# Revit family: Sanitary_Installation-Systems_DURAVIT-AG_DuraSystem-Actuator-Plate-WD5002
name_source: partatom
category: Generic Models
revit_build: Autodesk Revit 2018 (Build: 20180329_1100(x64)
units: mm (PartAtom-declared; Revit-internal decimal feet)

## family parameters
Can host rebar = No
Cut with Voids When Loaded = No
Host = Face
OmniClass Number = 23.31.19.00
OmniClass Title = Toilets
Part Type = Normal
Room Calculation Point = No
Round Connector Dimension = Use Diameter
Shared = No

## types (1)
- DuraSystem Actuator Plate WD5002
    BIMobject category = Installation Systems
    Date of publishing = 26/05/2020 00:00:00
    Default Elevation = 1219 mm
    Description = Actuator Plate A1, for toilet, glass white, mechanical actuation, 157x230x14 mm
    Design country = Germany
    EAN code = 4053424507316
    ETIM classification = EC012353 | Accessories bathroom accessories
    Edition number = 1
    IFC Classification = Actuator
    Installation instructions = http://pro.duravit.com
    Main material = Duravit - Metal - 00 - White Alpin
    Manufacturer = Duravit
    Manufacturer country = Germany
    Manufacturer name = DURAVIT AG
    Masterformat 2014 Code = 22 40 00
    Masterformat 2014 Description = Plumbing Fixtures
    Material main = Glass
    Model = DuraSystem Actuator Plate WD5002
    NBS Reference Code = 35-93-62
    NBS Reference Description = Pre-Plumbed Installation Frames
    OmniClass Code = 23-31 19 00
    OmniClass Description = Toilets
    Product Guid = 8d7ea177-b607-4225-b3c1-5c3097dd7139
    Product SKU = DuraSystem-actuator-plate-WD5002
    Product certification = http://pro.duravit.com
    Product data url = https://bimobject.com
    Product family = DuraSystem
    Product group = Mechanical flush plate for WC
    Product name = DuraSystem Actuator Plate WD5002
    Product url = http://pro.duravit.com
    QR code = https://bimobject.com
    Technical description = http://pro.duravit.com
    UNSPSC Code = 3018
    URL = https://www.duravit.com
    Uniclass 1.4 Code = L7216
    Uniclass 1.4 Description = Toilets
    Uniclass 2.0 Code = PR-35-93-62
    Uniclass 2.0 Description = Pre-Plumbed Installation Frames
    Uniclass 2015 Code = Pr_40_20_93_62
    Uniclass 2015 Name = Pre-plumbed installation frames
    Uniformat II Code = D2010
    Uniformat II Description = Plumbing Fixtures
    Weight Net (Kg) = 0.7
    Youtube clip = http://pro.duravit.com

## geometry (parser evidence)
native form markers: Sweep x3
no freeform markers — native parametric forms only
